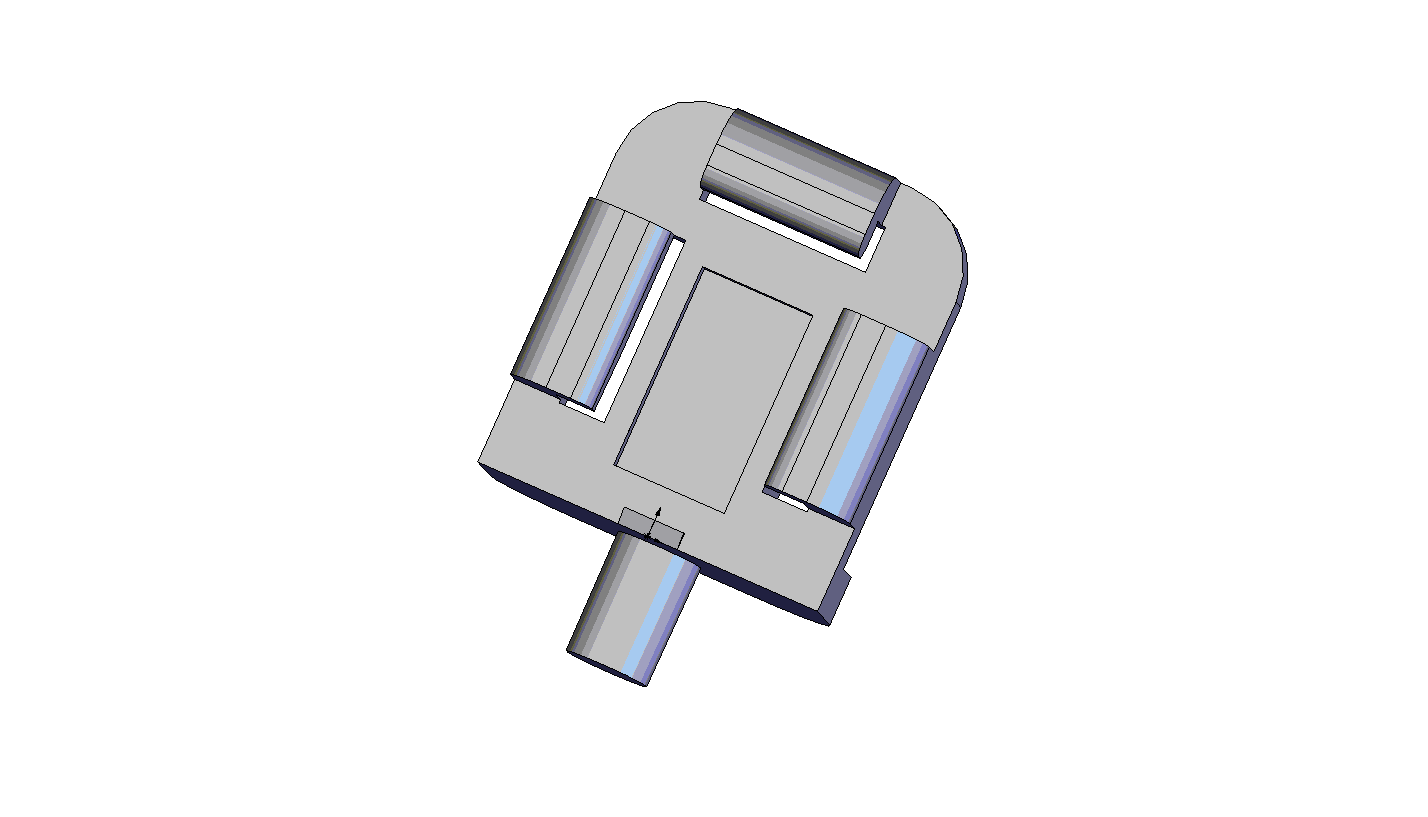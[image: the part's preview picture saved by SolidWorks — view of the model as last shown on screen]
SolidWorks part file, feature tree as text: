
SOLIDWORKS PART (.sldprt)
format: sldprt  version: not decoded by parser v0  size: 388,608 bytes
history: native  units: mm
features: sketch x9, extrude x6, fillet x5, cut_extrude x3, material x1, chamfer x1 (+11 scaffold rows collapsed)
feature tree (36):
  scaffold x11  (default folders/planes/origin — collapsed)
  material  "Material <not specified>"
  sketch  "Sketch1"  dims[D1=4.3mm D2=9.8mm]
  extrude  "Extrude1"  Depth=1.2mm
  sketch  "Sketch2"  dims[D1=1.2mm]
  extrude  "Extrude2"  Depth=3.9mm
  fillet  "Fillet1"  Radius=2mm
  sketch  "Sketch3"  dims[D1=4.46mm D2=2.085mm D3=4.0mm D4=2.0mm D5=2.03mm D6=2.12mm D7=2.12mm D8=4.36mm]
  extrude  "Extrude3"  Depth=2.1mm
  sketch  "Sketch4"  dims[c1.D1=2.3mm c1.D2=2.3mm c1.D3=1.14mm c1.D4=1.14mm c1.D5=1.14mm c1.D6=2.3mm c1.D7=4.6mm c1.D8=4.6mm c1.D9=2.1mm c1.D10=4.2mm c1.D11=2.0mm c1.D12=2.0mm c2.D6=1.07mm]
  cut_extrude  "Cut-Extrude1"  Depth=2.06mm
  fillet  "Fillet2"  Radius=1mm
  fillet  "Fillet3"  Radius=0.5mm
  sketch  "Sketch5"  dims[D1=2.8mm D2=1.4mm D3=1.2mm D4=5.0mm]
  cut_extrude  "Cut-Extrude2"  Depth=0.5mm
  sketch  "Sketch6"  dims[D1=0.2mm D2=0.4mm]
  extrude  "Extrude4"  Depth=1.5mm
  sketch  "Sketch7"  dims[D1=7.2mm]
  extrude  "Extrude6"  [1 undecoded]
  fillet  "Fillet5"  Radius=2mm
  fillet  "Fillet4"  Radius=0.3mm
  sketch  "Sketch8"  dims[D2=2.1mm D1=3.0mm]
  extrude  "Extrude7"  Depth=3mm
  sketch  "Sketch10"  dims[D1=1.0mm D2=1.5mm]
  cut_extrude  "Cut-Extrude3"  Depth=6.28mm
  chamfer  "Chamfer1"  Distance=0.25mm Angle=45deg
decode coverage: 23 of 24 modeling features carry decoded parameters
note: 1 parameter value undecoded
note: suppression state not decoded; provenance and decode notes live in map.json
